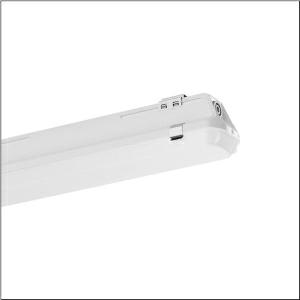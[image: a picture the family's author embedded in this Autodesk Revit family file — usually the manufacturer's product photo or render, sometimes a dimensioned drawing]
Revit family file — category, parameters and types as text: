
# Revit family: monsun_r__11_parking_51fg207p440h_0f51
name_source: partatom
category: Lighting Fixtures
units: mm (PartAtom-declared; Revit-internal decimal feet)

## family parameters
Cut with Voids When Loaded = No
Host = Face
Light Source = No
Part Type = Normal
Room Calculation Point = No
Round Connector Dimension = Use Diameter
Shared = No

## types (1)
- Monsun® 11 parking (1 x LED, 4820 lm, 29.2 W, 4000K)
    Apparent Load = 29 VA
    CIE Flux Codes = 45 75 93 94 100
    Color Rendering = 80
    Color Temperature = 4000K
    Default Elevation = 1800 mm
    Description = Monsun® 11 parking, damp-proof luminaire, chain hanger, primary optical cover: enclosure, of PC, light emission: direct distribution, primary light characteristic: symmetric, installation type: suspended mounting, surface-mounted, horizontal mounting, vertical mounting, LED, rated luminous flux: 4.820lm, luminous efficacy: 165lm/W, light colour: 840, colour temperature: 4000K, control gear: ECG, with terminal, 3-pole, max. 2.5mm², mains connection: 220..240V, AC, 50/60Hz, rated input power: 29W, housing, of glass-fibre reinforced polyester, uncoated, bright grey, incl. chain hanger, length: 1.590mm, width: 90mm, height: 88mm, clip for enclosure, of stainless steel (V2A), ceiling mounting element, of stainless steel (V2A), chain hanger, of stainless steel (V2A), protection rating (complete): IP66, insulation class (complete): insulation class I (protective earthing), certification: CE, ENEC, VDE, UKCA, protection symbol: D, impact resistance: IK08, permissible operating ambient temperature: -35..+40°C, standard: EN 50419, EN 60598-2-1, no direct snow, no direct sun, no direct rain, for indoor or canopied outdoor use, corresponds to IFS (International Featured Standards) requirements for safety and quality in the food industry, contact your sales advisor before using the luminaires in applications with unclear chemical exposure, large temperature fluctuations or condensation-forming humidity, LABS conformity tested according to VDMA 24364:2018-05, packaging unit: 1 piece
    Height = 89 mm
    Lamp = 1 x LED
    Lamp Light Flux = 4820 lm
    Lamp Power = 29.2 W
    Lamp count = 1
    Length = 1590 mm
    Luminous efficacy = 165 lm/W
    Manufacturer = Siteco
    ModVariant = No
    Model = 51FG207P440H
    Mounting Place = Ceiling
    Mounting Type = Surface mounted
    Number of Poles = 1
    OnlyDefault = Yes
    Power Factor = 1
    Product Name = Monsun® 11 parking
    Product group = damp-proof luminaire
    ProductGroupID = 300
    Protection Class = Protection class I
    Protection Degree = IP 66
    RLX_Detail_Level = 1
    RLX_Emergency_Light_Flux = 0 lm
    RLX_Emergency_Type = 0
    RLX_Emergency_Type_DB = No
    RlxData = <blob elided: 88625 chars, md5=186db083>
    Socket = socket
    Standby Power = 0 W
    System Light Flux = 4820 lm
    System Power = 29 W
    Type Comments = Product without accessories
    Type Image = l_1004748.jpg
    URL = http://relux.com
    VarID = ---
    Voltage = 0 V
    Weight = 0.00 kg
    Width = 90 mm

## geometry (parser evidence)
native form markers: Blend x4, Sweep x12
no freeform markers — native parametric forms only
